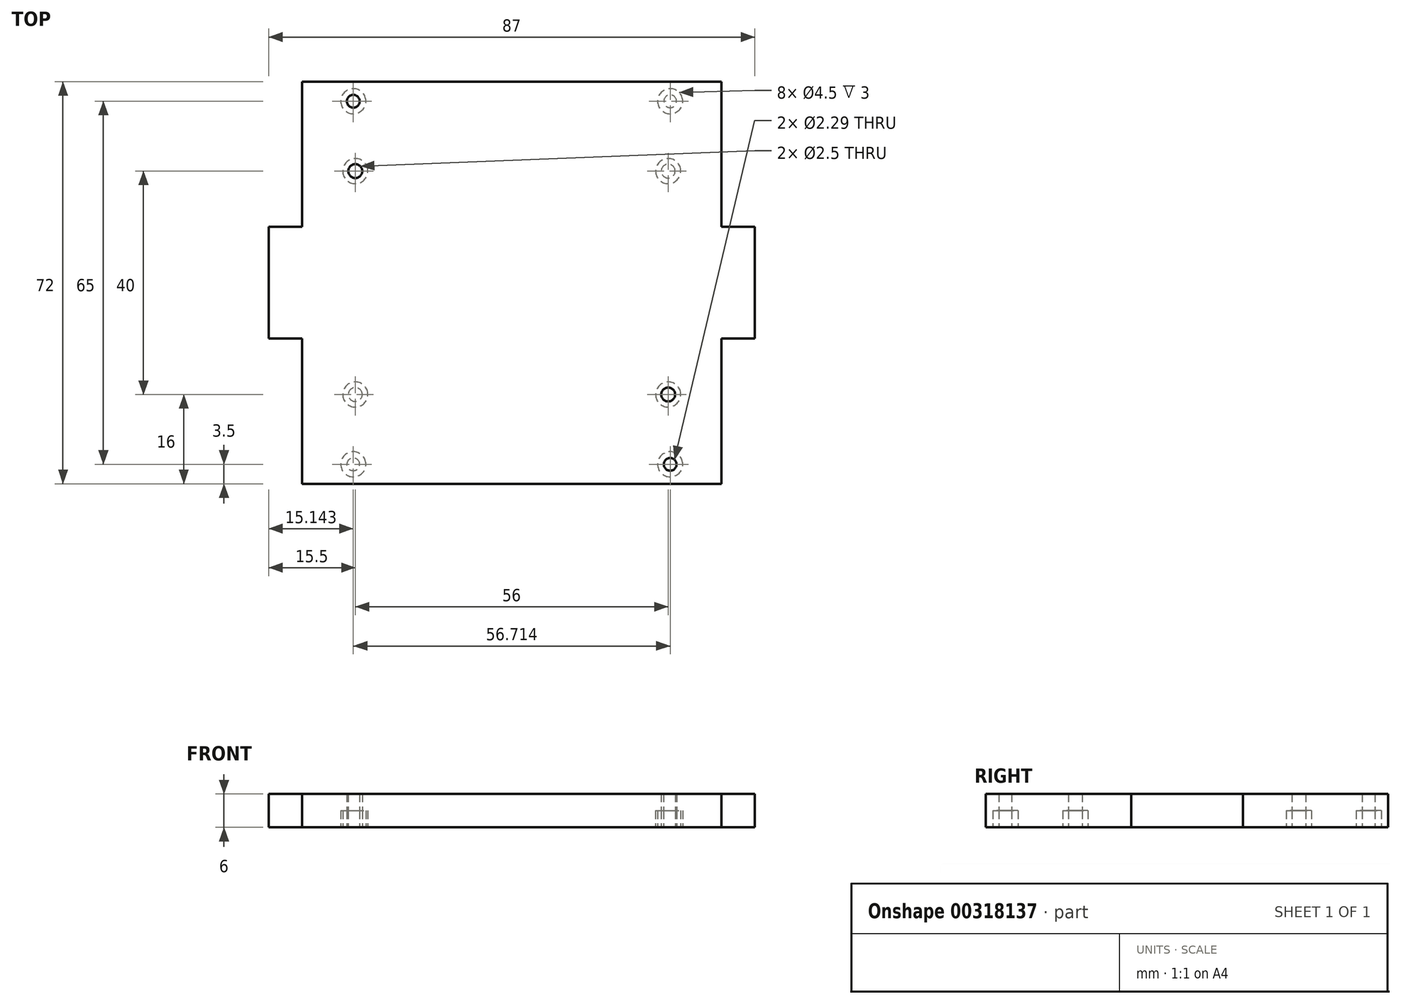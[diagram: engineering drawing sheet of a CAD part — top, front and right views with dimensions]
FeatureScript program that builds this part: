
annotation { "Feature Type Name" : "Feature", "Feature Type Description" : "" }
export const myFeature = defineFeature(function(context is Context, id is Id, definition is map)
    precondition{}
    {
        {
            var Q0;
            Q0=qCreatedBy(makeId("Top.planeOp"),FACE);
            var sketch = newSketch(context, id + "F0", { "sketchPlane" : qUnion([Q0])});
            skLineSegment(sketch, "E0.bottom", {"start": v(37.5, -36) * mm, "end": v(-37.5, -36) * mm});
            skLineSegment(sketch, "E0.top", {"start": v(37.5, 36) * mm, "end": v(-37.5, 36) * mm});
            skLineSegment(sketch, "E0.left", {"start": v(37.5, -36) * mm, "end": v(37.5, 36) * mm});
            skLineSegment(sketch, "E0.right", {"start": v(-37.5, -36) * mm, "end": v(-37.5, 36) * mm});
            skPoint(sketch, "E0.middle", {"position": v(0, 0) * mm});
            skLineSegment(sketch, "E1", {"start": v(-37.5, 10) * mm, "end": v(-43.5, 10) * mm});
            skLineSegment(sketch, "E2", {"start": v(-43.5, 10) * mm, "end": v(-43.5, -10) * mm});
            skLineSegment(sketch, "E3", {"start": v(-43.5, -10) * mm, "end": v(-37.5, -10) * mm});
            skLineSegment(sketch, "E4", {"start": v(37.5, 0) * mm, "end": v(-37.5, 0) * mm, "construction": true});
            skLineSegment(sketch, "E5", {"start": v(0, 36) * mm, "end": v(0, -36) * mm, "construction": true});
            skLineSegment(sketch, "E6.MirrorCS", {"start": v(43.5, -10) * mm, "end": v(37.5, -10) * mm});
            skLineSegment(sketch, "E7.MirrorCS", {"start": v(43.5, 10) * mm, "end": v(43.5, -10) * mm});
            skLineSegment(sketch, "E8.MirrorCS", {"start": v(37.5, 10) * mm, "end": v(43.5, 10) * mm});
            skSolve(sketch);
        }
        {
            var Q0;
            Q0 = qSketchRegion(id + "F0", true);
            extrude(context, id + "F1", {"entities" : qUnion([Q0]), "depth" : 6 * mm});
        }
        {
            var Q0;
            Q0=makeQuery(id+"F1.opExtrude","CAP_FACE",FACE,{"disambiguationData":[OSD([sQuery(id+"F0.wireOp",EDGE,"E0.bottom"),sQuery(id+"F0.wireOp",EDGE,"E0.top"),sQuery(id+"F0.wireOp",EDGE,"E0.left"),sQuery(id+"F0.wireOp",EDGE,"E0.right"),sQuery(id+"F0.wireOp",EDGE,"E1"),sQuery(id+"F0.wireOp",EDGE,"E2"),sQuery(id+"F0.wireOp",EDGE,"E3"),sQuery(id+"F0.wireOp",EDGE,"E6.MirrorCS"),sQuery(id+"F0.wireOp",EDGE,"E7.MirrorCS"),sQuery(id+"F0.wireOp",EDGE,"E8.MirrorCS")])],"isStart":true});
            var sketch = newSketch(context, id + "F2", { "sketchPlane" : qUnion([Q0])});
            skLineSegment(sketch, "E9", {"start": v(-43.5, 0) * mm, "end": v(43.5, 0) * mm, "construction": true});
            skLineSegment(sketch, "E10", {"start": v(0, 36) * mm, "end": v(0, -36) * mm, "construction": true});
            skCircle(sketch, "E11", {"center": v(-28, -20) * mm, "radius": 2.25 * mm});
            skLineSegment(sketch, "E12.bottom", {"start": v(-21, 21) * mm, "end": v(21, 21) * mm, "construction": true});
            skLineSegment(sketch, "E12.top", {"start": v(-21, -21) * mm, "end": v(21, -21) * mm, "construction": true});
            skLineSegment(sketch, "E12.left", {"start": v(-21, 21) * mm, "end": v(-21, -21) * mm, "construction": true});
            skLineSegment(sketch, "E12.right", {"start": v(21, 21) * mm, "end": v(21, -21) * mm, "construction": true});
            skPoint(sketch, "E12.middle", {"position": v(0, 0) * mm});
            skCircle(sketch, "E13.MirrorC", {"center": v(28, -20) * mm, "radius": 2.25 * mm});
            skCircle(sketch, "E14.MirrorC", {"center": v(-28, 20) * mm, "radius": 2.25 * mm});
            skCircle(sketch, "E15.MirrorC", {"center": v(28, 20) * mm, "radius": 2.25 * mm});
            skCircle(sketch, "E16", {"center": v(-28, -20) * mm, "radius": 1.25 * mm});
            skCircle(sketch, "E17.MirrorC", {"center": v(28, -20) * mm, "radius": 1.25 * mm});
            skCircle(sketch, "E18.MirrorC", {"center": v(-28, 20) * mm, "radius": 1.25 * mm});
            skCircle(sketch, "E19.MirrorC", {"center": v(28, 20) * mm, "radius": 1.25 * mm});
            skCircle(sketch, "E20", {"center": v(-28.36, -32.5) * mm, "radius": 2.25 * mm});
            skCircle(sketch, "E21.MirrorC", {"center": v(28.36, -32.5) * mm, "radius": 2.25 * mm});
            skCircle(sketch, "E22.MirrorC", {"center": v(-28.36, 32.5) * mm, "radius": 2.25 * mm});
            skCircle(sketch, "E23.MirrorC", {"center": v(28.36, 32.5) * mm, "radius": 2.25 * mm});
            skCircle(sketch, "E24", {"center": v(-28.36, -32.5) * mm, "radius": 1.14 * mm});
            skCircle(sketch, "E25.MirrorC", {"center": v(-28.36, 32.5) * mm, "radius": 1.14 * mm});
            skCircle(sketch, "E26.MirrorC", {"center": v(28.36, 32.5) * mm, "radius": 1.14 * mm});
            skCircle(sketch, "E27.MirrorC", {"center": v(28.36, -32.5) * mm, "radius": 1.14 * mm});
            skSolve(sketch);
        }
        {
            var Q0;
            Q0 = qSketchRegion(id + "F2", true);
            extrude(context, id + "F3", {"entities" : qUnion([Q0]), "operationType" : NewBodyOperationType.REMOVE, "oppositeDirection" : true, "depth" : 3 * mm});
        }
        {
            var Q0;
            Q0=makeQuery(id+"F2.imprint","IMPRINT",FACE,{"disambiguationData":[TD([[makeQuery(id+"F2.imprint","IMPRINT",EDGE,{"derivedFrom":sQuery(id+"F2.wireOp",EDGE,"E18.MirrorC")}),-1.0]])]});
            var Q1;
            Q1=makeQuery(id+"F2.imprint","IMPRINT",FACE,{"disambiguationData":[TD([[makeQuery(id+"F2.imprint","IMPRINT",EDGE,{"derivedFrom":sQuery(id+"F2.wireOp",EDGE,"E16")}),1.0]])]});
            var Q2;
            Q2=makeQuery(id+"F2.imprint","IMPRINT",FACE,{"disambiguationData":[TD([[makeQuery(id+"F2.imprint","IMPRINT",EDGE,{"derivedFrom":sQuery(id+"F2.wireOp",EDGE,"E17.MirrorC")}),-1.0]])]});
            var Q3;
            Q3=makeQuery(id+"F2.imprint","IMPRINT",FACE,{"disambiguationData":[TD([[makeQuery(id+"F2.imprint","IMPRINT",EDGE,{"derivedFrom":sQuery(id+"F2.wireOp",EDGE,"E19.MirrorC")}),1.0]])]});
            var Q4;
            Q4=makeQuery(id+"F2.imprint","IMPRINT",FACE,{"disambiguationData":[TD([[makeQuery(id+"F2.imprint","IMPRINT",EDGE,{"derivedFrom":sQuery(id+"F2.wireOp",EDGE,"E24")}),1.0]])]});
            var Q5;
            Q5=makeQuery(id+"F2.imprint","IMPRINT",FACE,{"disambiguationData":[TD([[makeQuery(id+"F2.imprint","IMPRINT",EDGE,{"derivedFrom":sQuery(id+"F2.wireOp",EDGE,"E27.MirrorC")}),-1.0]])]});
            var Q6;
            Q6=makeQuery(id+"F2.imprint","IMPRINT",FACE,{"disambiguationData":[TD([[makeQuery(id+"F2.imprint","IMPRINT",EDGE,{"derivedFrom":sQuery(id+"F2.wireOp",EDGE,"E26.MirrorC")}),1.0]])]});
            var Q7;
            Q7=makeQuery(id+"F2.imprint","IMPRINT",FACE,{"disambiguationData":[TD([[makeQuery(id+"F2.imprint","IMPRINT",EDGE,{"derivedFrom":sQuery(id+"F2.wireOp",EDGE,"E25.MirrorC")}),-1.0]])]});
            extrude(context, id + "F4", {"entities" : qUnion([Q0, Q1, Q2, Q3, Q4, Q5, Q6, Q7]), "operationType" : NewBodyOperationType.REMOVE, "endBound" : BoundingType.UP_TO_NEXT, "oppositeDirection" : true, "depth" : 25 * mm});
        }
    });
